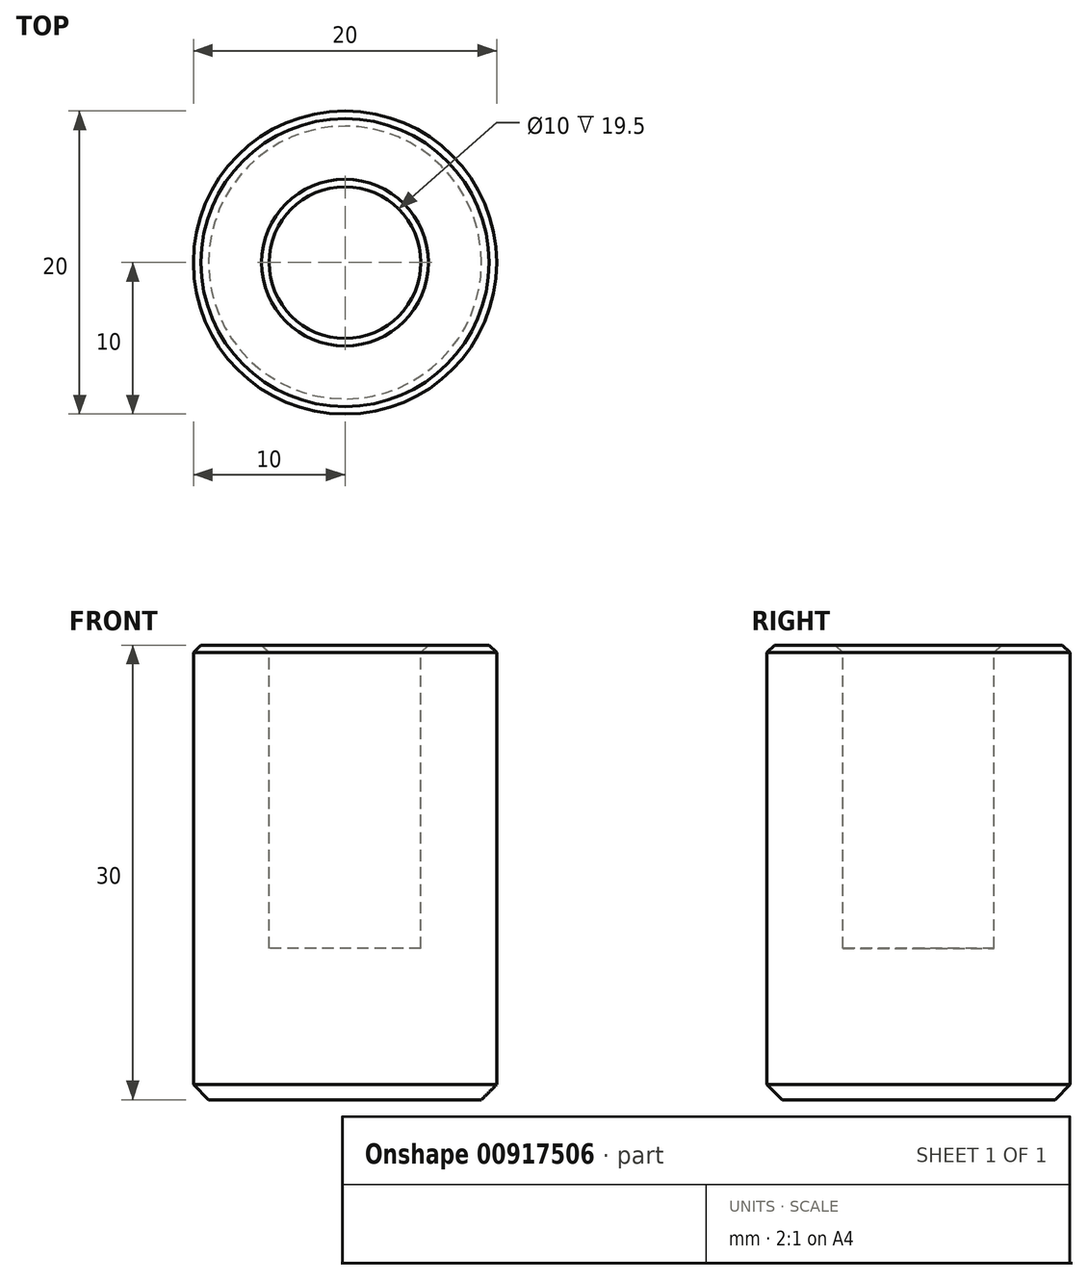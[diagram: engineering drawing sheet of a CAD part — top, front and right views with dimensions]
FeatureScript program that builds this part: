
annotation { "Feature Type Name" : "Feature", "Feature Type Description" : "" }
export const myFeature = defineFeature(function(context is Context, id is Id, definition is map)
    precondition{}
    {
        {
            var Q0;
            Q0=qCreatedBy(makeId("Front.planeOp"),FACE);
            var sketch = newSketch(context, id + "F0", { "sketchPlane" : qUnion([Q0])});
            skLineSegment(sketch, "E0", {"start": v(0, -30) * mm, "end": v(10, -30) * mm});
            skLineSegment(sketch, "E1", {"start": v(10, 0) * mm, "end": v(10, -30) * mm});
            skLineSegment(sketch, "E2", {"start": v(10, 0) * mm, "end": v(5, 0) * mm});
            skLineSegment(sketch, "E3", {"start": v(5, 0) * mm, "end": v(5, -20) * mm});
            skLineSegment(sketch, "E4", {"start": v(5, -20) * mm, "end": v(0, -20) * mm});
            skLineSegment(sketch, "E5", {"start": v(0, -20) * mm, "end": v(0, -30) * mm, "construction": true});
            skLineSegment(sketch, "E6", {"start": v(0, -20) * mm, "end": v(0, -30) * mm});
            skSolve(sketch);
        }
        {
            var Q0;
            Q0=qSketchRegion(id+"F0",true);
            var Q1;
            Q1=sQuery(id+"F0.wireOp",EDGE,"E5");
            revolve(context, id + "F1", {"surfaceOperationType" : NewSurfaceOperationType.NEW, "entities" : qUnion([Q0]), "axis" : qUnion([Q1]), "revolveType" : RevolveType.FULL});
        }
        {
            var Q0;
            Q0=makeQuery(id+"F1.opRevolve","SWEPT_EDGE",EDGE,{"disambiguationData":[OSD([sQuery(id+"F0.wireOp",EDGE,"E0"),sQuery(id+"F0.wireOp",EDGE,"E1")])]});
            chamfer(context, id + "F2", {"entities" : qUnion([Q0]), "width" : 1 * mm, "tangentPropagation" : true});
        }
        {
            var Q0;
            Q0=makeQuery(id+"F1.opRevolve","SWEPT_EDGE",EDGE,{"disambiguationData":[OSD([sQuery(id+"F0.wireOp",EDGE,"E1"),sQuery(id+"F0.wireOp",EDGE,"E2")])]});
            var Q1;
            Q1=makeQuery(id+"F1.opRevolve","SWEPT_EDGE",EDGE,{"disambiguationData":[OSD([sQuery(id+"F0.wireOp",EDGE,"E2"),sQuery(id+"F0.wireOp",EDGE,"E3")])]});
            chamfer(context, id + "F3", {"entities" : qUnion([Q0, Q1]), "width" : 0.5 * mm, "tangentPropagation" : true});
        }
    });
